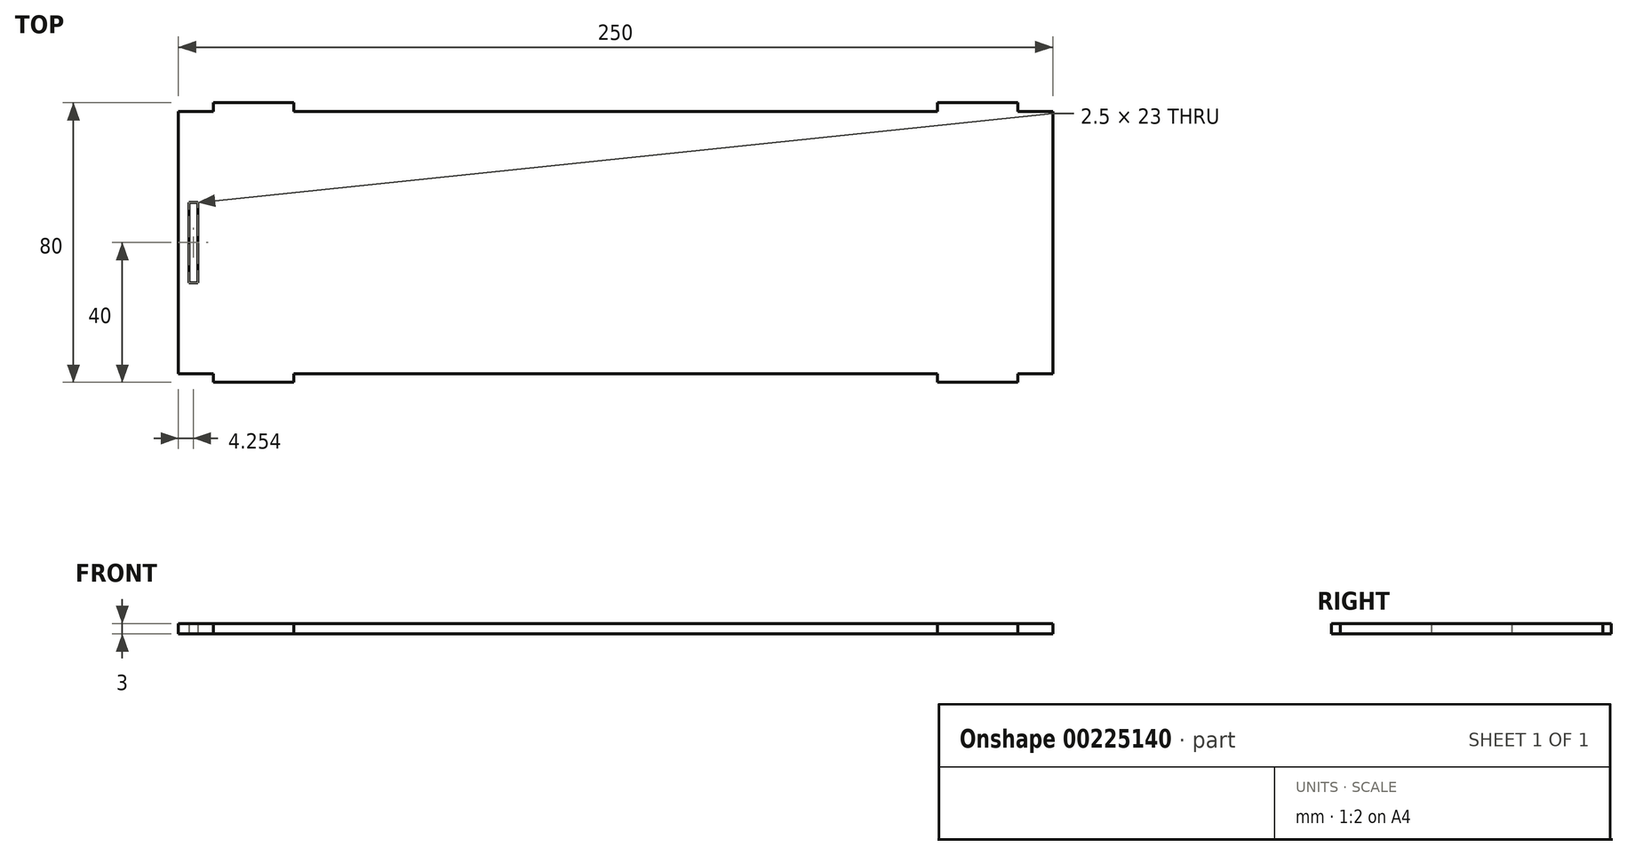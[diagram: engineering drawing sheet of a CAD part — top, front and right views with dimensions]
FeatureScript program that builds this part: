
annotation { "Feature Type Name" : "Feature", "Feature Type Description" : "" }
export const myFeature = defineFeature(function(context is Context, id is Id, definition is map)
    precondition{}
    {
        {
            var Q0;
            Q0=qCreatedBy(makeId("Top.planeOp"),FACE);
            var sketch = newSketch(context, id + "F0", { "sketchPlane" : qUnion([Q0])});
            skLineSegment(sketch, "E0.bottom", {"start": v(-112.65, -77.5) * mm, "end": v(137.35, -77.5) * mm});
            skLineSegment(sketch, "E0.top", {"start": v(-112.65, -2.5) * mm, "end": v(137.35, -2.5) * mm});
            skLineSegment(sketch, "E0.left", {"start": v(-112.65, -77.5) * mm, "end": v(-112.65, -2.5) * mm});
            skLineSegment(sketch, "E0.right", {"start": v(137.35, -77.5) * mm, "end": v(137.35, -2.5) * mm});
            skLineSegment(sketch, "E1.bottom", {"start": v(-102.65, -2.5) * mm, "end": v(-79.65, -2.5) * mm});
            skLineSegment(sketch, "E1.top", {"start": v(-102.65, 0) * mm, "end": v(-79.65, 0) * mm});
            skLineSegment(sketch, "E1.left", {"start": v(-102.65, -2.5) * mm, "end": v(-102.65, 0) * mm});
            skLineSegment(sketch, "E1.right", {"start": v(-79.65, -2.5) * mm, "end": v(-79.65, 0) * mm});
            skLineSegment(sketch, "E2.bottom", {"start": v(104.35, -2.5) * mm, "end": v(127.35, -2.5) * mm});
            skLineSegment(sketch, "E2.top", {"start": v(104.35, 0) * mm, "end": v(127.35, 0) * mm});
            skLineSegment(sketch, "E2.left", {"start": v(104.35, -2.5) * mm, "end": v(104.35, 0) * mm});
            skLineSegment(sketch, "E2.right", {"start": v(127.35, -2.5) * mm, "end": v(127.35, 0) * mm});
            skLineSegment(sketch, "E3.bottom", {"start": v(-102.65, -77.5) * mm, "end": v(-79.65, -77.5) * mm});
            skLineSegment(sketch, "E3.top", {"start": v(-102.65, -80) * mm, "end": v(-79.65, -80) * mm});
            skLineSegment(sketch, "E3.left", {"start": v(-102.65, -77.5) * mm, "end": v(-102.65, -80) * mm});
            skLineSegment(sketch, "E3.right", {"start": v(-79.65, -77.5) * mm, "end": v(-79.65, -80) * mm});
            skLineSegment(sketch, "E4.bottom", {"start": v(104.35, -77.5) * mm, "end": v(127.35, -77.5) * mm});
            skLineSegment(sketch, "E4.top", {"start": v(104.35, -80) * mm, "end": v(127.35, -80) * mm});
            skLineSegment(sketch, "E4.left", {"start": v(104.35, -77.5) * mm, "end": v(104.35, -80) * mm});
            skLineSegment(sketch, "E4.right", {"start": v(127.35, -77.5) * mm, "end": v(127.35, -80) * mm});
            skLineSegment(sketch, "E5", {"start": v(-112.65, -2.5) * mm, "end": v(-102.65, -2.5) * mm});
            skLineSegment(sketch, "E6", {"start": v(127.35, -2.5) * mm, "end": v(137.35, -2.5) * mm});
            skLineSegment(sketch, "E7", {"start": v(-112.65, -77.5) * mm, "end": v(-102.65, -77.5) * mm});
            skLineSegment(sketch, "E8", {"start": v(127.35, -77.5) * mm, "end": v(137.35, -77.5) * mm});
            skLineSegment(sketch, "E9.bottom", {"start": v(-109.65, -28.5) * mm, "end": v(-107.15, -28.5) * mm});
            skLineSegment(sketch, "E9.top", {"start": v(-109.65, -51.5) * mm, "end": v(-107.15, -51.5) * mm});
            skLineSegment(sketch, "E9.left", {"start": v(-109.65, -28.5) * mm, "end": v(-109.65, -51.5) * mm});
            skLineSegment(sketch, "E9.right", {"start": v(-107.15, -28.5) * mm, "end": v(-107.15, -51.5) * mm});
            skSolve(sketch);
        }
        {
            var Q0;
            Q0 = qSketchRegion(id + "F0", true);
            extrude(context, id + "F1", {"entities" : qUnion([Q0]), "depth" : 3 * mm});
        }
    });
